# Revit family: QF_Vollrath_5950280
name_source: partatom
category: Specialty Equipment
revit_build: Autodesk Revit 2016 (Build: 20151007_0715(x64)
units: mm (PartAtom-declared; Revit-internal decimal feet)

## family parameters
Always vertical = Yes
Cut with Voids When Loaded = No
OmniClass Number = 23.40.40.00
OmniClass Title = Food Service Equipment and Furnishings
Part Type = Normal
Room Calculation Point = No
Round Connector Dimension = Use Diameter
Shared = No
Work Plane-Based = Yes

## types (2) — shared parameters
Apparent Power = 312 VA
Conn Plug = NEMA 5-15P
Default Elevation = 0.00"
Depth = 16.06"
Description = Countertop Induction Range
Elec Conn Connection Height = 2.00"
FL Amps = 3 A
Foodservice Equipment Identifier = Yes
Manufacturer = Vollrath
Model = 5950280
Phase = 1
Volts = 120 V
Watts = 300 W
Width = 16.06"
zero-valued in all types: Weight in Pounds

## per-type parameters (varying)
| type | Cycle |
| 120/50/1 | 50 Hz |
| 120/60/1 | 60 Hz |

## geometry (parser evidence)
native form markers: Blend x4, Sweep x3
no freeform markers — native parametric forms only
